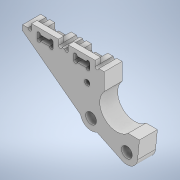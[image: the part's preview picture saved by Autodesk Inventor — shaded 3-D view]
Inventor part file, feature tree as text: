
AUTODESK INVENTOR PART (.ipt)
format: ipt  version: 2020.2 (Build 242310000, 310)  size: 452,096 bytes
history: native  units: mm
features: extrude x9, sketch x8, projected_geometry x5, hole x2, other x1
ambient origin geometry x8: Origin, YZ Plane, XZ Plane, XY Plane, X Axis, Y Axis, Z Axis, Center Point
bodies: Body1 (feature_tree)
feature tree (25):
  other  "ソリッド1"
  sketch  "スケッチ1"
  sketch  "スケッチ2"
  extrude  "押し出し1"  Depth=6.0mm
  hole  "穴1"  [1 undecoded]
  sketch  "スケッチ3"
  sketch  "スケッチ4"
  extrude  "押し出し2"  Depth=3.0mm
  extrude  "押し出し3"  Depth=3.0mm
  hole  "穴2"  [1 undecoded]
  extrude  "押し出し4"  Depth=14.0mm
  extrude  "押し出し5"  Depth=10.0mm TaperAngle=0.0deg
  extrude  "押し出し6"  Depth=9.0mm
  extrude  "押し出し7"  Depth=10.0mm TaperAngle=0.0deg
  sketch  "スケッチ8"
  extrude  "押し出し8"  Depth=10.0mm TaperAngle=0.0deg
  extrude  "押し出し9"  Depth=10.0mm TaperAngle=0.0deg
  projected_geometry  "投影ループ1"
  sketch  "スケッチ5"
  projected_geometry  "投影ループ2"
  sketch  "スケッチ6"
  projected_geometry  "投影ループ3"
  sketch  "スケッチ7"
  projected_geometry  "投影ループ4"
  projected_geometry  "投影ループ5"
note: 2 required parameter values undecoded (feature->parameter linkage not recoverable at this tier; creation-order binding heuristic only, values carry confidence <= 0.55)
